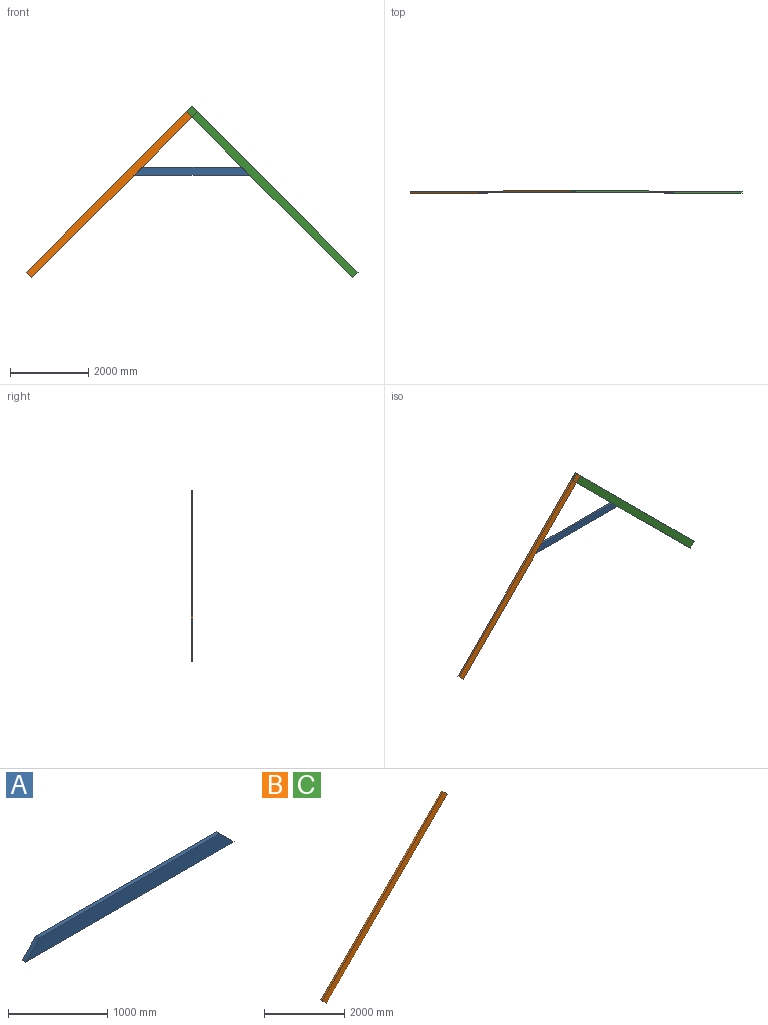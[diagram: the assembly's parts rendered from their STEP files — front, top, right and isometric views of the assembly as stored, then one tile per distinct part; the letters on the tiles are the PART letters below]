
ASSEMBLY  parts=3 mates=6
PART A: 6 faces, bbox 2965.7x50x200 mm
  f0: plane 2965.69x50mm, normal (0,0,-1), area 148284.3mm2, adj f1,f3,f4,f5
  f1: plane 200x200mm, normal (0.71,0,0.71), area 14142.1mm2, adj f0,f2,f4,f5
  f2: plane 2565.69x50mm, normal (0,0,1), area 128284.3mm2, adj f1,f3,f4,f5
  f3: plane 200x200mm, normal (-0.71,0,0.71), area 14142.1mm2, adj f0,f2,f4,f5
  f4: plane 2965.69x200mm, normal (0,-1,0), area 553137.1mm2, adj f0,f1,f2,f3
  f5: plane 2965.69x200mm, normal (0,1,0), area 553137.1mm2, adj f0,f1,f2,f3
PART B: 6 faces, bbox 4384.1x50x4384.1 mm
  f0: plane 4242.64x4242.64mm, normal (0.71,0,-0.71), area 300000mm2, adj f1,f3,f4,f5
  f1: plane 141.42x141.42mm, normal (0.71,0,0.71), area 10000mm2, adj f0,f2,f4,f5
  f2: plane 4242.64x4242.64mm, normal (-0.71,0,0.71), area 300000mm2, adj f1,f3,f4,f5
  f3: plane 141.42x141.42mm, normal (-0.71,0,-0.71), area 10000mm2, adj f0,f2,f4,f5
  f4: plane 4384.06x4384.06mm, normal (0,-1,0), area 1200000mm2, adj f0,f1,f2,f3
  f5: plane 4384.06x4384.06mm, normal (0,1,0), area 1200000mm2, adj f0,f1,f2,f3
PART C: same geometry as B
PLACE A t=(0,25,-2800)mm
PLACE B t=(0,25,-2517.16)mm
PLACE C rot(axis=(0,-1,0),90deg) t=(3941.42,25,1424.26)mm
MATE planar C.f5 <-> A.f5  axis (0,1,0) through (2050.61,25,-626.35)mm
MATE planar B.f2 <-> C.f1  axis (-0.71,0,0.71) through (0,25,1565.69)mm
MATE planar C.f0 <-> B.f1  axis (0.71,0,0.71) through (2121.32,0,-555.63)mm
MATE planar A.f1 <-> C.f2  axis (0.71,0,0.71) through (1382.84,0,-100)mm
MATE planar A.f3 <-> B.f0  axis (-0.71,0,0.71) through (-1382.84,0,-100)mm
MATE planar B.f5 <-> A.f5  axis (0,1,0) through (-2050.61,25,-626.35)mm
